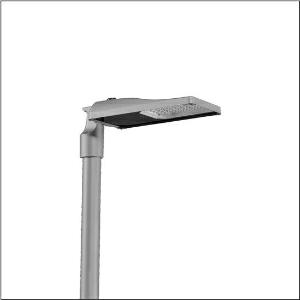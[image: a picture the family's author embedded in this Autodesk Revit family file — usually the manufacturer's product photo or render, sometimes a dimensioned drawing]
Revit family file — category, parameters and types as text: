
# Revit family: streetlight_sl_31_mini___st1_0a_5xh2d31s08ha_0250
name_source: partatom
category: Lighting Fixtures
units: mm (PartAtom-declared; Revit-internal decimal feet)

## family parameters
Cut with Voids When Loaded = No
Host = Face
Light Source = No
Part Type = Normal
Room Calculation Point = No
Round Connector Dimension = Use Diameter
Shared = No

## types (1)
- --- (1 x LED, 9230 lm, 68.2 W, 3000K)
    Apparent Load = 68 VA
    CIE Flux Codes = 37 72 97 100 100
    Color Rendering = 70
    Color Temperature = 3000K
    Default Elevation = 1800 mm
    Description = Streetlight SL 31 mini, mast luminaire, primary light control with lens, of PMMA, primary optical cover: cover, of toughened safety glass, transparent, light distribution: ST1.0a, light emission: direct distribution, primary light characteristic: asymmetric, installation type: post-top, side-entry, LED, High Power LED, rated luminous flux: 9.230lm, luminous efficacy: 135lm/W, light colour: 730, colour temperature: 3000K, control: presetting dimming logarithmic, flexible luminous flux parameterisation, time-dependent luminous flux control, constant luminous flux control, power reduction, intelligent temperature release in ECG and LED module, overheat protection, with cable H07RN-F 2x 1.5mm², mains connection: 220..240V, AC, 50/60Hz, connection cable pre-assembled, cable length: 8,5m, start of lifetime: 68W, end of service life: 74W, reduction: 30W, luminaire housing, of diecast aluminium, powder-coated, Siteco® metallic grey (DB 702S), corrosivity category C5 high according to DIN EN ISO 12944, no sealing on luminaire upper side, inclination: -15°..+20° (post-top) | -20°..+20° (side-entry), adjustable in 5° steps, mast flange (76/60mm) included as standard, multi-level sealing system, sealing non-destructively replaceable, Smart Interface above, protection rating (complete): IP66, insulation class (complete): insulation class II (safety insulation), certification: CE, ENEC, ENEC+, VDE, UKCA, ZD4i, impact resistance: IK09, permissible operating ambient temperature for outdoor applications: -40..+50°C, standard-compliant lighting for roads and squares, packaging unit: 1 piece

Light Distribution: ST1.0a
    Height = 76 mm
    Lamp = 1 x LED
    Lamp Light Flux = 9230 lm
    Lamp Power = 68.2 W
    Lamp count = 1
    Length = 547 mm
    Luminous efficacy = 135 lm/W
    Manufacturer = Siteco
    ModVariant = No
    Model = 5XH2D31S08HA
    Number of Poles = 1
    OnlyDefault = Yes
    Power Factor = 1
    Product Name = Streetlight SL 31 mini | ST1.0a
    Product group = mast luminaire | pylon top
    ProductGroupID = 6100
    Protection Class = Protection class II
    Protection Degree = IP 66
    RLX_Detail_Level = 1
    RLX_Emergency_Light_Flux = 0 lm
    RLX_Emergency_Type = 0
    RLX_Emergency_Type_DB = No
    RlxData = <blob elided: 39705 chars, md5=7dabc0e2>
    Socket = socket
    Standby Power = 0 W
    System Light Flux = 9230 lm
    System Power = 68 W
    Type Comments = factory setting: luminous flux: 100 % | dim-lin: 254 | 692 mA
    Type Image = l_1300330.jpg
    URL = http://relux.com
    VarID = @adj_013001
    Voltage = 0 V
    Weight = 0.00 kg
    Width = 265 mm

## geometry (parser evidence)
native form markers: Blend x4, Sweep x9
no freeform markers — native parametric forms only
